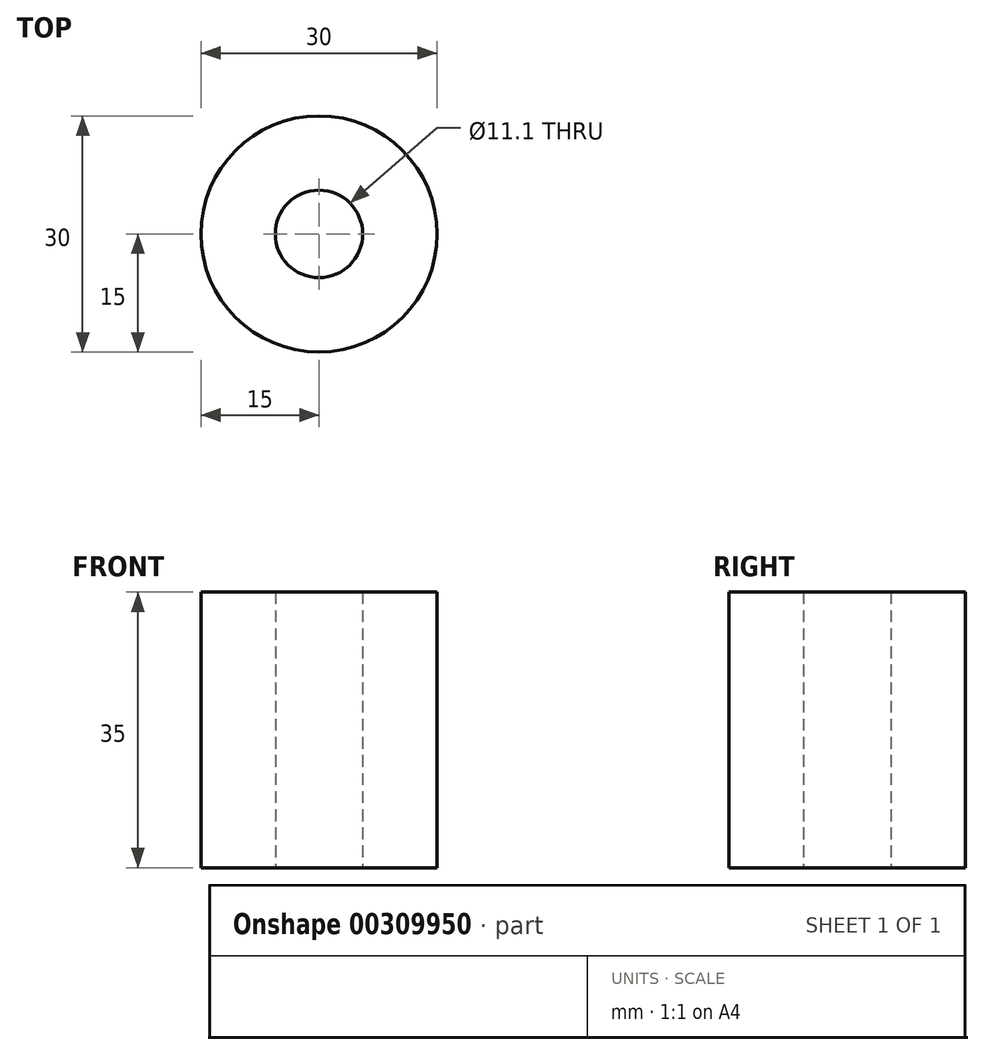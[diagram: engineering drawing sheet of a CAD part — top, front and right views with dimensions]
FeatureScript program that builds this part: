
annotation { "Feature Type Name" : "Feature", "Feature Type Description" : "" }
export const myFeature = defineFeature(function(context is Context, id is Id, definition is map)
    precondition{}
    {
        {
            var Q0;
            Q0=qCreatedBy(makeId("Top.planeOp"),FACE);
            var sketch = newSketch(context, id + "F0", { "sketchPlane" : qUnion([Q0])});
            skCircle(sketch, "E0", {"center": v(0, 0) * mm, "radius": 15 * mm});
            skCircle(sketch, "E1", {"center": v(0, 0) * mm, "radius": 5.55 * mm});
            skSolve(sketch);
        }
        {
            var Q0;
            Q0=makeQuery(id+"F0.imprint","IMPRINT",FACE,{"disambiguationData":[TD([[makeQuery(id+"F0.imprint","IMPRINT",EDGE,{"derivedFrom":sQuery(id+"F0.wireOp",EDGE,"E0")}),1.0]])]});
            extrude(context, id + "F1", {"entities" : qUnion([Q0]), "depth" : 35 * mm});
        }
    });
